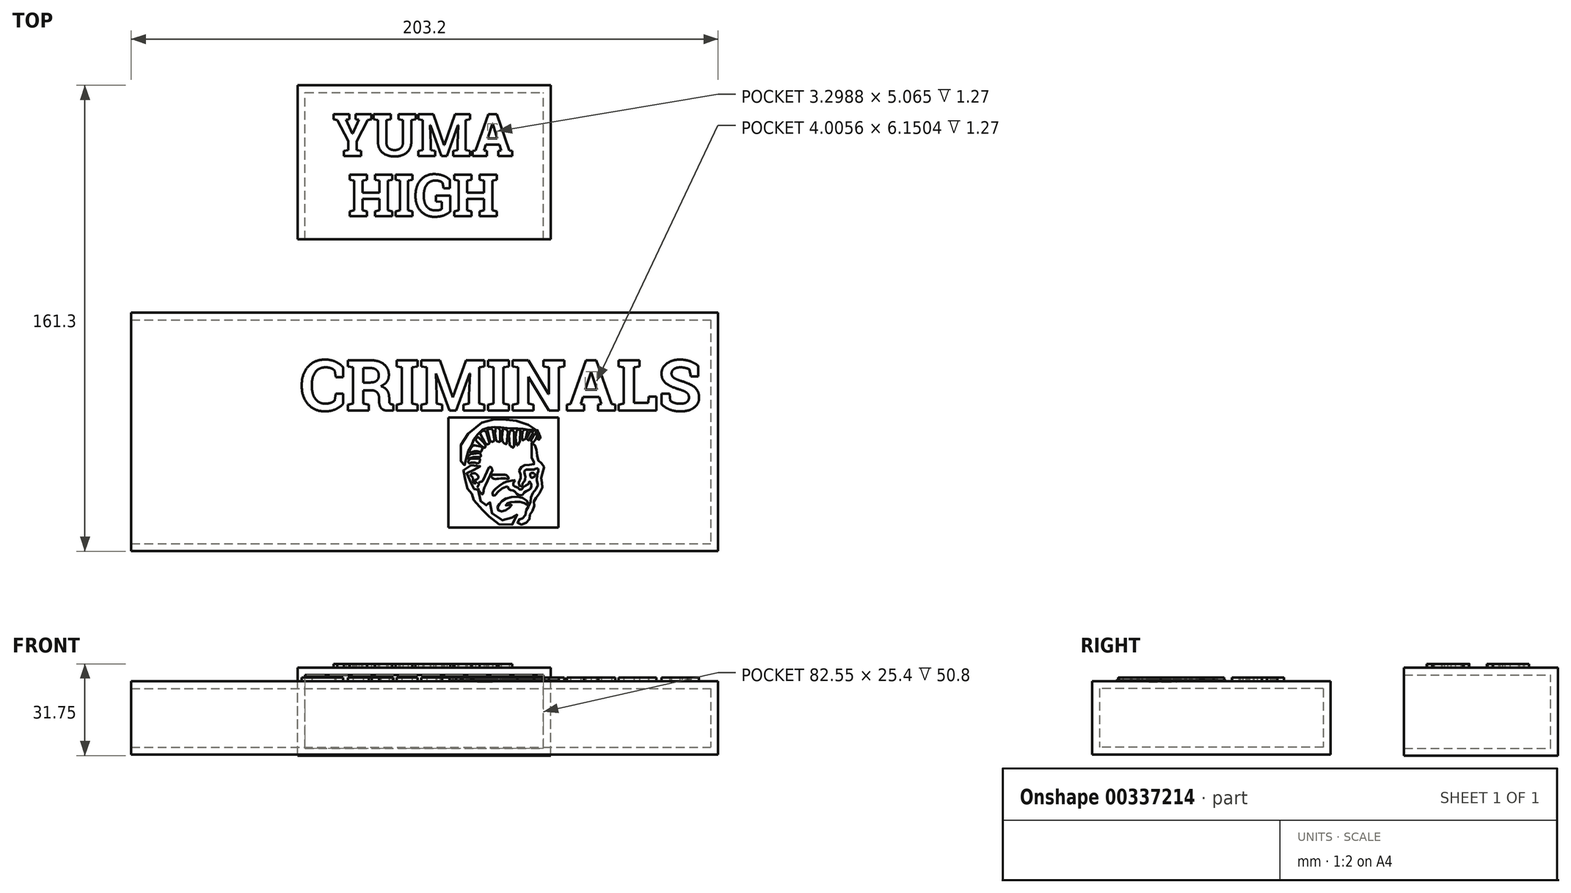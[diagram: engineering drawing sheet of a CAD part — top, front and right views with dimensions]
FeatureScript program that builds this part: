
annotation { "Feature Type Name" : "Feature", "Feature Type Description" : "" }
export const myFeature = defineFeature(function(context is Context, id is Id, definition is map)
    precondition{}
    {
        {
            var Q0;
            Q0=qCreatedBy(makeId("Top.planeOp"),FACE);
            var sketch = newSketch(context, id + "F0", { "sketchPlane" : qUnion([Q0])});
            skLineSegment(sketch, "E0.bottom", {"start": v(-101.6, 41.27) * mm, "end": v(101.6, 41.27) * mm});
            skLineSegment(sketch, "E0.top", {"start": v(-101.6, -41.27) * mm, "end": v(101.6, -41.27) * mm});
            skLineSegment(sketch, "E0.left", {"start": v(-101.6, 41.27) * mm, "end": v(-101.6, -41.27) * mm});
            skLineSegment(sketch, "E0.right", {"start": v(101.6, 41.27) * mm, "end": v(101.6, -41.28) * mm});
            skPoint(sketch, "E0.middle", {"position": v(0, 0) * mm});
            skSolve(sketch);
        }
        {
            var Q0;
            Q0 = qSketchRegion(id + "F0", true);
            extrude(context, id + "F1", {"entities" : qUnion([Q0]), "depth" : 25.4 * mm});
        }
        {
            var Q0;
            Q0=makeQuery(id+"F1.opExtrude","SWEPT_FACE",FACE,{"disambiguationData":[OSD([sQuery(id+"F0.wireOp",EDGE,"E0.left")])]});
            shell(context, id + "F2", {"entities" : qUnion([Q0]), "thickness" : 2.54 * mm});
        }
        {
            var Q0;
            Q0=qCreatedBy(makeId("Right.planeOp"),FACE);
            var sketch = newSketch(context, id + "F3", { "sketchPlane" : qUnion([Q0])});
            skLineSegment(sketch, "E1.bottom", {"start": v(41.28, -47.48) * mm, "end": v(-41.27, -47.48) * mm});
            skLineSegment(sketch, "E1.top", {"start": v(41.27, -72.88) * mm, "end": v(-41.27, -72.88) * mm});
            skLineSegment(sketch, "E1.left", {"start": v(41.28, -47.48) * mm, "end": v(41.27, -72.88) * mm});
            skLineSegment(sketch, "E1.right", {"start": v(-41.27, -47.48) * mm, "end": v(-41.28, -72.88) * mm});
            skPoint(sketch, "E1.middle", {"position": v(0, -60.18) * mm});
            skSolve(sketch);
        }
        {
            var Q0;
            Q0=makeQuery(id+"F3.imprint","IMPRINT",FACE,{"disambiguationData":[TD([[makeQuery(id+"F3.imprint","IMPRINT",EDGE,{"derivedFrom":sQuery(id+"F3.wireOp",EDGE,"E1.bottom")}),1.0]])]});
            extrude(context, id + "F4", {"entities" : qUnion([Q0]), "depth" : 50.8 * mm});
        }
        {
            var Q0;
            Q0=makeQuery(id+"F4.opExtrude","CAP_FACE",FACE,{"disambiguationData":[OSD([sQuery(id+"F3.wireOp",EDGE,"E1.bottom"),sQuery(id+"F3.wireOp",EDGE,"E1.top"),sQuery(id+"F3.wireOp",EDGE,"E1.left"),sQuery(id+"F3.wireOp",EDGE,"E1.right")])],"isStart":false});
            shell(context, id + "F5", {"entities" : qUnion([Q0]), "thickness" : 2.54 * mm, "oppositeDirection" : true});
        }
        {
            var Q0;
            Q0=makeQuery(id+"F4.opExtrude","SWEPT_BODY",BODY,{"disambiguationData":[OSD([sQuery(id+"F3.wireOp",EDGE,"E1.bottom"),sQuery(id+"F3.wireOp",EDGE,"E1.top"),sQuery(id+"F3.wireOp",EDGE,"E1.left"),sQuery(id+"F3.wireOp",EDGE,"E1.right")])]});
            var Q1;
            Q1=makeQuery(id+"F4.opExtrude","CAP_EDGE",EDGE,{"disambiguationData":[OSD([sQuery(id+"F3.wireOp",EDGE,"E1.left")])],"isStart":true});
            transform(context, id + "F6", {"entities" : qUnion([Q0]), "transformType" : TransformType.ROTATION, "transformAxis" : qUnion([Q1]), "angle" : 270 * degree, "makeCopy" : false});
        }
        {
            var Q0;
            Q0=makeQuery(id+"F4.opExtrude","SWEPT_BODY",BODY,{"disambiguationData":[OSD([sQuery(id+"F3.wireOp",EDGE,"E1.bottom"),sQuery(id+"F3.wireOp",EDGE,"E1.top"),sQuery(id+"F3.wireOp",EDGE,"E1.left"),sQuery(id+"F3.wireOp",EDGE,"E1.right")])]});
            transform(context, id + "F7", {"entities" : qUnion([Q0]), "transformType" : TransformType.TRANSLATION_3D, "dx" : -40.9 * mm, "dy" : -81.28 * mm, "dz" : 0 * mm, "makeCopy" : false});
        }
        {
            var Q0;
            Q0=makeQuery(id+"F4.opExtrude","SWEPT_FACE",FACE,{"disambiguationData":[OSD([sQuery(id+"F3.wireOp",EDGE,"E1.top")])]});
            var sketch = newSketch(context, id + "F8", { "sketchPlane" : qUnion([Q0])});
            skText(sketch, "E2", { "text": "YUMA", "fontName": "RobotoSlab-Bold.ttf"});
            skText(sketch, "E3", { "text": "HIGH", "fontName": "RobotoSlab-Bold.ttf"});
            const initialGuessF8  = {"E2": [-0.03137, 0.01307, 1, 0, 0.01456], "E3": [-0.02597, -0.00784, 1, 0, 0.01456]};
            skSetInitialGuess(sketch, initialGuessF8);
            skSolve(sketch);
        }
        {
            var Q0;
            Q0 = qSketchRegion(id + "F8", true);
            extrude(context, id + "F9", {"entities" : qUnion([Q0]), "operationType" : NewBodyOperationType.ADD, "depth" : 1.27 * mm});
        }
        {
            var Q0;
            Q0=makeQuery(id+"F1.opExtrude","CAP_FACE",FACE,{"disambiguationData":[OSD([sQuery(id+"F0.wireOp",EDGE,"E0.bottom"),sQuery(id+"F0.wireOp",EDGE,"E0.top"),sQuery(id+"F0.wireOp",EDGE,"E0.left"),sQuery(id+"F0.wireOp",EDGE,"E0.right")])],"isStart":false});
            var sketch = newSketch(context, id + "F10", { "sketchPlane" : qUnion([Q0])});
            skLineSegment(sketch, "E4.bottom", {"start": v(101.6, -41.28) * mm, "end": v(-48.26, -41.28) * mm});
            skLineSegment(sketch, "E4.top", {"start": v(101.6, 41.27) * mm, "end": v(-48.26, 41.27) * mm});
            skLineSegment(sketch, "E4.left", {"start": v(101.6, -41.28) * mm, "end": v(101.6, 41.28) * mm});
            skLineSegment(sketch, "E4.right", {"start": v(-48.26, -41.28) * mm, "end": v(-48.26, 41.27) * mm});
            skSolve(sketch);
        }
        {
            var Q0;
            Q0=makeQuery(id+"F10.imprint","IMPRINT",FACE,{"disambiguationData":[TD([[makeQuery(id+"F10.imprint","IMPRINT",EDGE,{"derivedFrom":sQuery(id+"F10.wireOp",EDGE,"E4.bottom")}),1.0]])]});
            var sketch = newSketch(context, id + "F11", { "sketchPlane" : qUnion([Q0])});
            skText(sketch, "E5", { "text": "CRIMINALS", "fontName": "RobotoSlab-Bold.ttf"});
            const initialGuessF11  = {"E5": [-0.04318, 0.00738, 1, 0, 0.01768]};
            skSetInitialGuess(sketch, initialGuessF11);
            skSolve(sketch);
        }
        {
            var Q0;
            Q0 = qSketchRegion(id + "F11", true);
            extrude(context, id + "F12", {"entities" : qUnion([Q0]), "operationType" : NewBodyOperationType.ADD, "depth" : 1.27 * mm});
        }
        {
            var Q0;
            Q0=makeQuery(id+"F10.imprint","IMPRINT",FACE,{"disambiguationData":[TD([[makeQuery(id+"F10.imprint","IMPRINT",EDGE,{"derivedFrom":sQuery(id+"F10.wireOp",EDGE,"E4.bottom")}),1.0]])]});
            var sketch = newSketch(context, id + "F13", { "sketchPlane" : qUnion([Q0])});
            skLineSegment(sketch, "E6", {"start": v(25.41, -10.64) * mm, "end": v(30.12, -12.8) * mm});
            skFitSpline(sketch, "E7", {"points": [v(30.12, -12.8) * mm, v(30.12, -13.45) * mm, v(29.01, -13.93) * mm], "startDerivative": vector(0.4, -1.7) * mm, "endDerivative": vector(-2.47, -0.63) * mm});
            skLineSegment(sketch, "E8", {"start": v(29.01, -13.93) * mm, "end": v(23.79, -11.55) * mm});
            skFitSpline(sketch, "E9", {"points": [v(23.79, -11.55) * mm, v(22.65, -11.03) * mm, v(20.72, -10.58) * mm, v(20.68, -10.32) * mm, v(21.24, -9.96) * mm, v(21.33, -9.63) * mm, v(21.67, -9.48) * mm, v(21.88, -9.52) * mm, v(22.1, -9.12) * mm, v(22.33, -9.04) * mm, v(22.6, -9.15) * mm, v(22.79, -8.94) * mm, v(22.93, -8.81) * mm, v(23.24, -8.8) * mm, v(23.79, -9.08) * mm, v(24.23, -9.3) * mm, v(24.36, -9.1) * mm, v(25.04, -9.8) * mm, v(25.02, -10.23) * mm, v(25.41, -10.64) * mm], "startDerivative": vector(-10.89, 6.86) * mm, "endDerivative": vector(9.47, -7.22) * mm});
            skLineSegment(sketch, "E10", {"start": v(17.4, -4.64) * mm, "end": v(19.45, -5.08) * mm});
            skFitSpline(sketch, "E11", {"points": [v(19.45, -5.08) * mm, v(19.86, -5.3) * mm, v(19.97, -5.88) * mm, v(19.73, -6.51) * mm, v(19.45, -6.88) * mm, v(18.23, -6.72) * mm, v(17.48, -6.64) * mm, v(16.69, -6.83) * mm, v(15.64, -6.91) * mm, v(16.64, -4.8) * mm, v(17.4, -4.64) * mm], "startDerivative": vector(6.4, -2.15) * mm, "endDerivative": vector(7.37, -1.37) * mm});
            skLineSegment(sketch, "E12", {"start": v(17.84, -3.06) * mm, "end": v(19.34, -4.6) * mm});
            skLineSegment(sketch, "E13", {"start": v(19.34, -4.6) * mm, "end": v(20.32, -5.26) * mm});
            skFitSpline(sketch, "E14", {"points": [v(20.32, -5.26) * mm, v(20.63, -5.4) * mm, v(21.12, -4.82) * mm, v(18.67, -1.85) * mm, v(18.63, -1.8) * mm, v(18.1, -2) * mm, v(17.68, -2.49) * mm, v(17.84, -3.06) * mm], "startDerivative": vector(2.61, -2.11) * mm, "endDerivative": vector(2.16, -4.54) * mm});
            skLineSegment(sketch, "E15", {"start": v(15.97, -7.65) * mm, "end": v(18.94, -7.28) * mm});
            skFitSpline(sketch, "E16", {"points": [v(18.94, -7.28) * mm, v(19.17, -7.38) * mm, v(19.47, -8.2) * mm, v(19.2, -8.63) * mm, v(18.65, -8.7) * mm], "startDerivative": vector(1.32, -0.15) * mm, "endDerivative": vector(-2.32, 0.1) * mm});
            skLineSegment(sketch, "E17", {"start": v(18.65, -8.7) * mm, "end": v(16.82, -8.7) * mm});
            skLineSegment(sketch, "E18", {"start": v(16.82, -8.7) * mm, "end": v(15.1, -9.24) * mm});
            skFitSpline(sketch, "E19", {"points": [v(15.1, -9.24) * mm, v(14.9, -9.12) * mm, v(15.1, -8.44) * mm, v(15.97, -7.65) * mm], "startDerivative": vector(-1.28, 0.36) * mm, "endDerivative": vector(2.2, 1.6) * mm});
            skLineSegment(sketch, "E20", {"start": v(15.97, -9.25) * mm, "end": v(19.01, -9.25) * mm});
            skFitSpline(sketch, "E21", {"points": [v(19.01, -9.25) * mm, v(19.15, -9.38) * mm, v(18.9, -10.7) * mm], "startDerivative": vector(0.63, -0.29) * mm, "endDerivative": vector(-0.65, -2.3) * mm});
            skLineSegment(sketch, "E22", {"start": v(18.9, -10.7) * mm, "end": v(18.18, -10.8) * mm});
            skLineSegment(sketch, "E23", {"start": v(18.18, -10.8) * mm, "end": v(17.35, -10.6) * mm});
            skLineSegment(sketch, "E24", {"start": v(17.35, -10.6) * mm, "end": v(16.02, -10.6) * mm});
            skFitSpline(sketch, "E25", {"points": [v(16.02, -10.6) * mm, v(15.56, -10.8) * mm, v(15.16, -10.6) * mm, v(15.32, -9.7) * mm, v(15.97, -9.25) * mm], "startDerivative": vector(-2.04, -1.27) * mm, "endDerivative": vector(2.65, 1.08) * mm});
            skLineSegment(sketch, "E26", {"start": v(19.29, -0.72) * mm, "end": v(20.96, -3.7) * mm});
            skLineSegment(sketch, "E27", {"start": v(22.5, -3.7) * mm, "end": v(21.33, 0) * mm});
            skFitSpline(sketch, "E28", {"points": [v(19.29, -0.72) * mm, v(19.29, -0.24) * mm, v(20.47, 0.44) * mm, v(21.33, 0) * mm], "startDerivative": vector(-0.61, 1.88) * mm, "endDerivative": vector(2.16, -2) * mm});
            skFitSpline(sketch, "E29", {"points": [v(20.96, -3.7) * mm, v(21.42, -4.26) * mm, v(22.2, -4.1) * mm, v(22.5, -3.7) * mm], "startDerivative": vector(1.03, -2.04) * mm, "endDerivative": vector(0.68, 1.49) * mm});
            skLineSegment(sketch, "E30", {"start": v(21.75, 0.27) * mm, "end": v(22.6, -2.8) * mm});
            skLineSegment(sketch, "E31", {"start": v(24.12, -2.43) * mm, "end": v(23.55, 0.6) * mm});
            skLineSegment(sketch, "E32", {"start": v(24.62, 1.4) * mm, "end": v(24.38, -0.65) * mm});
            skLineSegment(sketch, "E33", {"start": v(24.38, -0.65) * mm, "end": v(24.69, -2.8) * mm});
            skLineSegment(sketch, "E34", {"start": v(25.08, -3.25) * mm, "end": v(26.14, -3.55) * mm});
            skLineSegment(sketch, "E35", {"start": v(26.14, -3.55) * mm, "end": v(26.14, 0.6) * mm});
            skLineSegment(sketch, "E36", {"start": v(28.81, -0.22) * mm, "end": v(28.47, -3.92) * mm});
            skLineSegment(sketch, "E37", {"start": v(26.99, -3.33) * mm, "end": v(26.77, -1.87) * mm});
            skLineSegment(sketch, "E38", {"start": v(26.77, -1.87) * mm, "end": v(27, 0.57) * mm});
            skLineSegment(sketch, "E39", {"start": v(27.64, 1.07) * mm, "end": v(28.25, 0.76) * mm});
            skLineSegment(sketch, "E40", {"start": v(29.23, -1.06) * mm, "end": v(29.45, -4.37) * mm});
            skLineSegment(sketch, "E41", {"start": v(29.64, -4.83) * mm, "end": v(30.38, -5.33) * mm});
            skLineSegment(sketch, "E42", {"start": v(30.9, 0) * mm, "end": v(30.9, -4.98) * mm});
            skFitSpline(sketch, "E43", {"points": [v(21.75, 0.27) * mm, v(21.75, 0.68) * mm, v(22.41, 1.07) * mm, v(23.22, 0.98) * mm, v(23.55, 0.6) * mm], "startDerivative": vector(-0.5, 2.06) * mm, "endDerivative": vector(1.14, -1.93) * mm});
            skFitSpline(sketch, "E44", {"points": [v(22.6, -2.8) * mm, v(23.09, -3.29) * mm, v(23.9, -3.24) * mm, v(24.12, -2.43) * mm], "startDerivative": vector(1.23, -1.82) * mm, "endDerivative": vector(0.13, 2.8) * mm});
            skFitSpline(sketch, "E45", {"points": [v(24.62, 1.4) * mm, v(24.83, 1.61) * mm, v(25.18, 1.6) * mm, v(26.14, 0.6) * mm], "startDerivative": vector(0.79, 1.04) * mm, "endDerivative": vector(2.02, -2.51) * mm});
            skFitSpline(sketch, "E46", {"points": [v(27, 0.57) * mm, v(27.18, 1.07) * mm, v(27.64, 1.07) * mm], "startDerivative": vector(0.2, 1.2) * mm, "endDerivative": vector(1.1, -0.23) * mm});
            skFitSpline(sketch, "E47", {"points": [v(28.25, 0.76) * mm, v(28.66, 0.37) * mm, v(28.81, -0.22) * mm], "startDerivative": vector(0.97, -0.7) * mm, "endDerivative": vector(0.16, -1.25) * mm});
            skFitSpline(sketch, "E48", {"points": [v(26.99, -3.33) * mm, v(27.64, -3.98) * mm, v(28.25, -4.18) * mm, v(28.47, -3.92) * mm], "startDerivative": vector(1.46, -1.75) * mm, "endDerivative": vector(0.66, 1.36) * mm});
            skFitSpline(sketch, "E49", {"points": [v(29.23, -1.06) * mm, v(29.4, -0.22) * mm, v(29.6, 0.37) * mm, v(30.23, 0.57) * mm, v(30.69, 0.42) * mm, v(30.9, 0) * mm], "startDerivative": vector(0.82, 3.64) * mm, "endDerivative": vector(0.96, -2.68) * mm});
            skFitSpline(sketch, "E50", {"points": [v(30.38, -5.33) * mm, v(30.69, -5.33) * mm, v(30.9, -4.98) * mm], "startDerivative": vector(0.72, -0.15) * mm, "endDerivative": vector(0.34, 0.82) * mm});
            skLineSegment(sketch, "E51", {"start": v(24.69, -2.8) * mm, "end": v(25.08, -3.25) * mm});
            skLineSegment(sketch, "E52", {"start": v(29.45, -4.37) * mm, "end": v(29.64, -4.83) * mm});
            skLineSegment(sketch, "E53", {"start": v(33.17, 0.61) * mm, "end": v(32.95, -3.25) * mm});
            skLineSegment(sketch, "E54", {"start": v(32.95, -3.25) * mm, "end": v(32.23, -4.6) * mm});
            skLineSegment(sketch, "E55", {"start": v(32.23, -4.6) * mm, "end": v(31.95, -4.67) * mm});
            skLineSegment(sketch, "E56", {"start": v(31.95, -4.67) * mm, "end": v(31.71, -3.84) * mm});
            skLineSegment(sketch, "E57", {"start": v(31.71, -3.84) * mm, "end": v(31.5, -1.98) * mm});
            skLineSegment(sketch, "E58", {"start": v(31.5, -1.98) * mm, "end": v(31.69, 0) * mm});
            skLineSegment(sketch, "E59", {"start": v(34.02, 0.4) * mm, "end": v(33.74, -1.09) * mm});
            skLineSegment(sketch, "E60", {"start": v(33.74, -1.09) * mm, "end": v(33.74, -2.59) * mm});
            skLineSegment(sketch, "E61", {"start": v(35, -2.26) * mm, "end": v(35.54, 0) * mm});
            skLineSegment(sketch, "E62", {"start": v(35.54, 0) * mm, "end": v(35.54, 0.16) * mm});
            skLineSegment(sketch, "E63", {"start": v(36.3, -0.17) * mm, "end": v(35.54, -1.83) * mm});
            skLineSegment(sketch, "E64", {"start": v(36.2, -2.76) * mm, "end": v(37.33, -0.78) * mm});
            skLineSegment(sketch, "E65", {"start": v(36.85, -2.76) * mm, "end": v(38.1, -0.56) * mm});
            skLineSegment(sketch, "E66", {"start": v(37.57, -3.63) * mm, "end": v(38.48, -2.59) * mm});
            skLineSegment(sketch, "E67", {"start": v(38.48, -2.59) * mm, "end": v(38.9, -1.28) * mm});
            skLineSegment(sketch, "E68", {"start": v(38.9, -1.28) * mm, "end": v(38.64, -0.54) * mm});
            skLineSegment(sketch, "E69", {"start": v(38.64, -0.54) * mm, "end": v(38.1, -0.56) * mm});
            skLineSegment(sketch, "E70", {"start": v(38.55, 0.66) * mm, "end": v(38.1, 0.16) * mm});
            skLineSegment(sketch, "E71", {"start": v(38.1, 0.16) * mm, "end": v(37.45, 0.74) * mm});
            skLineSegment(sketch, "E72", {"start": v(37.45, 0.74) * mm, "end": v(36.22, 0.74) * mm});
            skFitSpline(sketch, "E73", {"points": [v(31.69, 0) * mm, v(32.1, 0.7) * mm, v(32.63, 0.85) * mm, v(33.17, 0.61) * mm], "startDerivative": vector(0.93, 2.18) * mm, "endDerivative": vector(1.66, -1) * mm});
            skFitSpline(sketch, "E74", {"points": [v(34.02, 0.4) * mm, v(34.32, 0.61) * mm, v(34.78, 0.8) * mm, v(35.33, 0.61) * mm, v(35.54, 0.16) * mm], "startDerivative": vector(1.32, 0.97) * mm, "endDerivative": vector(0.55, -1.97) * mm});
            skFitSpline(sketch, "E75", {"points": [v(33.74, -2.59) * mm, v(34.02, -2.8) * mm, v(35, -2.26) * mm], "startDerivative": vector(0.65, -0.87) * mm, "endDerivative": vector(1.77, 1.32) * mm});
            skFitSpline(sketch, "E76", {"points": [v(35.54, -1.83) * mm, v(35.33, -2.26) * mm, v(35.87, -2.78) * mm, v(36.2, -2.76) * mm], "startDerivative": vector(-1.16, -1.25) * mm, "endDerivative": vector(1.07, 0.37) * mm});
            skFitSpline(sketch, "E77", {"points": [v(36.3, -0.17) * mm, v(36.59, 0.16) * mm, v(37.33, -0.17) * mm, v(37.33, -0.78) * mm], "startDerivative": vector(0.68, 1.56) * mm, "endDerivative": vector(-0.55, -1.93) * mm});
            skFitSpline(sketch, "E78", {"points": [v(36.85, -2.76) * mm, v(37.02, -3.37) * mm, v(37.57, -3.63) * mm], "startDerivative": vector(0.15, -1.38) * mm, "endDerivative": vector(1.29, -0.36) * mm});
            skFitSpline(sketch, "E79", {"points": [v(36.22, 0.74) * mm, v(35.96, 0.74) * mm, v(35.24, 1.22) * mm, v(34.02, 1.1) * mm, v(33.37, 1.1) * mm, v(32.8, 1.35) * mm, v(32.28, 1.3) * mm, v(31.69, 0.92) * mm, v(31.06, 0.96) * mm, v(30.47, 1.14) * mm, v(29.75, 1.14) * mm, v(29.36, 0.92) * mm, v(28.8, 1) * mm, v(28.27, 1.53) * mm, v(27.36, 1.72) * mm, v(26.55, 1.57) * mm, v(25.48, 1.96) * mm, v(24.44, 2.07) * mm, v(24.18, 1.64) * mm, v(23.54, 1.42) * mm, v(22.8, 1.55) * mm, v(21.7, 1.4) * mm, v(21.28, 0.98) * mm, v(20.52, 0.92) * mm, v(19.69, 0.74) * mm, v(18.8, 0.16) * mm, v(18.47, -0.78) * mm, v(17.84, -1.37) * mm, v(17.38, -1.83) * mm, v(17.01, -2.59) * mm, v(16.97, -3.44) * mm, v(16.68, -4.16) * mm, v(16, -4.94) * mm, v(15.5, -5.42) * mm, v(15.12, -6.2) * mm, v(15.12, -7.27) * mm, v(14.72, -8.14) * mm, v(14.44, -8.95) * mm, v(14.46, -10.12) * mm, v(14.03, -11.17) * mm, v(13.44, -11.76) * mm, v(12.83, -11.39) * mm, v(12.57, -9.88) * mm, v(12.55, -4.55) * mm, v(12.57, -4.03) * mm, v(16.22, 0.74) * mm, v(20.26, 3.43) * mm, v(22.87, 4.14) * mm, v(24.37, 4.4) * mm, v(26.44, 4.47) * mm, v(29.31, 4.2) * mm, v(33.35, 3.45) * mm, v(35.84, 2.48) * mm, v(37.33, 1.72) * mm, v(38.55, 0.66) * mm], "startDerivative": vector(-27.73, -7.56) * mm, "endDerivative": vector(53.1, -52.46) * mm});
            skFitSpline(sketch, "E80", {"points": [v(33.87, -18.8) * mm, v(33.6, -18.88) * mm, v(32.86, -18.62) * mm, v(32.48, -18.17) * mm, v(32.62, -17.32) * mm, v(33.14, -16.23) * mm, v(33.4, -15.68) * mm, v(33.3, -15) * mm, v(32.98, -14.38) * mm, v(32.8, -13.29) * mm, v(33.21, -12.32) * mm, v(33.76, -11.83) * mm, v(34.49, -11.5) * mm, v(35.69, -11.39) * mm, v(36.78, -11.32) * mm, v(37.83, -11.16) * mm, v(38.07, -11.1) * mm, v(38.05, -10.82) * mm, v(37.5, -10.22) * mm, v(37, -8.5) * mm, v(37.05, -6.08) * mm, v(37.12, -4.9) * mm, v(36.96, -4.3) * mm, v(36.94, -3.86) * mm, v(37.15, -3.82) * mm, v(37.96, -4.42) * mm, v(38.5, -5.32) * mm, v(38.8, -6.88) * mm, v(39.03, -8.6) * mm, v(39.23, -9.61) * mm, v(40.06, -10.72) * mm, v(40.66, -10.98) * mm, v(41.33, -11.9) * mm, v(40.83, -14.16) * mm, v(40.46, -15.39) * mm, v(40.43, -16.37) * mm, v(40.66, -17.53) * mm], "startDerivative": vector(-14.66, -7.78) * mm, "endDerivative": vector(9.26, -38.03) * mm});
            skFitSpline(sketch, "E81", {"points": [v(40.66, -17.53) * mm, v(40.84, -18.51) * mm, v(40.25, -20.38) * mm, v(39.22, -21.92) * mm, v(38.39, -23.03) * mm, v(37.94, -23.68) * mm, v(37.87, -24.54) * mm, v(37.93, -25.66) * mm, v(37.58, -26.94) * mm, v(36.7, -28.13) * mm, v(36.37, -28.8) * mm, v(36.3, -29.87) * mm, v(36.03, -30.68) * mm, v(34.85, -31.52) * mm, v(33.83, -31.97) * mm, v(32.58, -31.96) * mm, v(32.14, -31.23) * mm, v(32.4, -30.5) * mm, v(33.03, -30.08) * mm, v(33.6, -30.02) * mm, v(34.3, -29.65) * mm, v(34.9, -28.73) * mm, v(35.07, -27.56) * mm, v(35.4, -26.63) * mm, v(35.92, -25.91) * mm, v(36.65, -24.7) * mm, v(36.74, -23.55) * mm, v(36.86, -22.48) * mm, v(37.2, -21.5) * mm, v(38.03, -20.45) * mm, v(38.8, -19.45) * mm, v(39.17, -18.62) * mm, v(38.94, -17.53) * mm, v(38.8, -16.2) * mm, v(38.92, -14.87) * mm], "startDerivative": vector(10.33, -31.8) * mm, "endDerivative": vector(5.32, 40.6) * mm});
            skFitSpline(sketch, "E82", {"points": [v(38.92, -14.87) * mm, v(39.3, -13.87) * mm, v(39.32, -12.74) * mm, v(38.92, -12.54) * mm, v(38.3, -12.84) * mm, v(37.42, -13.04) * mm, v(35.74, -13.05) * mm, v(34.89, -13.18) * mm, v(34.5, -14) * mm, v(34.77, -14.87) * mm, v(34.9, -15.88) * mm, v(34.5, -17.05) * mm, v(34.1, -17.53) * mm, v(33.8, -18.21) * mm, v(33.95, -18.57) * mm, v(33.87, -18.8) * mm], "startDerivative": vector(5.43, 12.1) * mm, "endDerivative": vector(-3.93, -6.24) * mm});
            skFitSpline(sketch, "E83", {"points": [v(36.54, -14.62) * mm, v(36.64, -14.37) * mm, v(37.28, -14.15) * mm, v(38, -14.48) * mm, v(38.29, -15.02) * mm, v(37.91, -15.56) * mm, v(36.95, -15.74) * mm, v(36.5, -15.19) * mm, v(36.54, -14.62) * mm]});
            skFitSpline(sketch, "E84", {"points": [v(35.77, -18.15) * mm, v(36.02, -17.84) * mm, v(36.16, -17.27) * mm, v(36.37, -17.16) * mm, v(36.64, -17.53) * mm, v(36.93, -18.51) * mm, v(36.58, -19.66) * mm, v(35.94, -20.18) * mm, v(35.16, -20.48) * mm, v(34.4, -21.02) * mm, v(34.08, -21.57) * mm, v(33, -21.97) * mm, v(31.87, -21.43) * mm, v(31.3, -20.75) * mm, v(30.77, -20.3) * mm, v(29.74, -20.12) * mm, v(29.07, -19.7) * mm, v(28.86, -18.8) * mm], "startDerivative": vector(7.08, 5.96) * mm, "endDerivative": vector(-1.6, 15.8) * mm});
            skFitSpline(sketch, "E85", {"points": [v(28.86, -18.8) * mm, v(28.62, -18.8) * mm, v(27.66, -19.2) * mm, v(25.87, -20.25) * mm, v(24.13, -22.08) * mm, v(23.76, -22.09) * mm, v(23.6, -21.64) * mm, v(23.52, -20.82) * mm, v(24.08, -20.1) * mm, v(24.92, -19.29) * mm, v(26.92, -17.9) * mm, v(28.24, -17.2) * mm, v(30.86, -16.7) * mm, v(31.16, -16.7) * mm, v(31.23, -16.92) * mm, v(31.04, -17.23) * mm, v(30.88, -17.32) * mm, v(30.74, -17.53) * mm, v(30.67, -18.04) * mm, v(30.76, -18.8) * mm, v(31.5, -18.8) * mm, v(32.44, -19.54) * mm, v(32.86, -19.92) * mm, v(33.37, -19.95) * mm, v(33.87, -19.53) * mm, v(34.31, -19) * mm, v(35.11, -18.51) * mm, v(35.77, -18.15) * mm], "startDerivative": vector(-10.06, 1.52) * mm, "endDerivative": vector(17.39, 10.06) * mm});
            skFitSpline(sketch, "E86", {"points": [v(23.06, -15.45) * mm, v(22.88, -15.13) * mm, v(22.93, -14.86) * mm, v(23.5, -14.74) * mm, v(24.25, -14.75) * mm, v(25.59, -14.78) * mm, v(27.12, -14.77) * mm, v(28.05, -14.8) * mm, v(28.7, -15.38) * mm, v(29.12, -16.02) * mm, v(28.86, -16.22) * mm, v(28.36, -16.15) * mm, v(27.4, -16.07) * mm, v(26, -16.12) * mm, v(25.13, -16.25) * mm, v(24.49, -16.34) * mm, v(23.68, -16.08) * mm, v(23.06, -15.45) * mm]});
            skFitSpline(sketch, "E87", {"points": [v(38.73, -0.24) * mm, v(38.55, 0.16) * mm, v(38.9, 0.66) * mm, v(39.09, 0.66) * mm, v(39.18, 0.16) * mm, v(39.49, -0.17) * mm, v(39.67, -0.5) * mm, v(39.63, -0.78) * mm, v(39.81, -1.01) * mm, v(39.87, -1.5) * mm, v(40.05, -1.84) * mm, v(39.91, -2.3) * mm, v(39.71, -2.38) * mm, v(39.68, -2.66) * mm, v(39.25, -2.5) * mm, v(39.15, -1.97) * mm, v(39.26, -1.63) * mm, v(39.35, -1.03) * mm, v(39.1, -0.6) * mm, v(38.73, -0.24) * mm]});
            skFitSpline(sketch, "E88", {"points": [v(18.54, -20.05) * mm, v(18.65, -19.41) * mm, v(18.47, -19.14) * mm, v(18.01, -19.41) * mm, v(17.26, -19.73) * mm, v(16.51, -19.82) * mm, v(16.13, -19.8) * mm, v(16.13, -18.7) * mm, v(15.95, -17.34) * mm, v(15.5, -16.1) * mm, v(14.7, -14.7) * mm, v(14.56, -13.78) * mm, v(15.04, -13.14) * mm, v(16.22, -13.1) * mm, v(17.56, -13.23) * mm, v(18.51, -13.16) * mm, v(19.2, -12.55) * mm, v(19.1, -11.55) * mm, v(17.97, -11.26) * mm, v(16.79, -11.3) * mm, v(15.76, -11.55) * mm, v(14.45, -11.55) * mm, v(13.65, -12.69) * mm, v(13.1, -13.91) * mm, v(13.31, -15.37) * mm, v(13.95, -16.41) * mm, v(14.38, -17.03) * mm, v(14.65, -17.69) * mm, v(14.74, -18.91) * mm, v(14.86, -20.53) * mm, v(15, -21.2) * mm, v(15.83, -21.52) * mm, v(16.4, -21.32) * mm, v(16.72, -21.27) * mm, v(16.88, -21.64) * mm, v(16.7, -22.1) * mm, v(17.13, -23.75) * mm, v(18.2, -25.3) * mm, v(19.83, -26.77) * mm, v(21.44, -27.84) * mm, v(21.72, -27.95) * mm, v(22.08, -28.84) * mm, v(22.78, -30.14) * mm, v(24.33, -31.34) * mm, v(26.6, -32.13) * mm, v(29.06, -32.2) * mm, v(30.49, -31.93) * mm, v(31.76, -30.64) * mm, v(32.15, -29.05) * mm, v(31.7, -28.25) * mm, v(31.26, -28.14) * mm, v(30.58, -28.7) * mm, v(30.15, -29.7) * mm, v(29.8, -30.27) * mm, v(28.44, -30.59) * mm, v(26.7, -30.54) * mm, v(24.99, -29.86) * mm, v(23.52, -28.45) * mm, v(22.92, -26.1) * mm, v(22.74, -24.93) * mm, v(22.58, -24.3) * mm, v(21.8, -23.91) * mm, v(21.38, -24) * mm, v(21.26, -24.86) * mm, v(21.33, -25.55) * mm, v(21.29, -25.73) * mm, v(20.99, -25.66) * mm, v(20.04, -24.68) * mm, v(18.95, -23.34) * mm, v(18.38, -21.82) * mm, v(18.54, -20.05) * mm]});
            skFitSpline(sketch, "E89", {"points": [v(17.4, -17.87) * mm, v(16.9, -17.48) * mm, v(16.72, -16.14) * mm, v(16.47, -15.55) * mm, v(15.92, -15.19) * mm, v(15.92, -14.75) * mm, v(16.8, -14.28) * mm, v(18.06, -14.64) * mm, v(18.58, -15.82) * mm, v(18.01, -16.4) * mm, v(17.54, -16.62) * mm, v(17.38, -17.07) * mm, v(17.72, -17.41) * mm, v(17.9, -17.34) * mm, v(17.8, -17.64) * mm, v(17.4, -17.87) * mm]});
            skFitSpline(sketch, "E90", {"points": [v(28.85, -25.36) * mm, v(28.12, -25.55) * mm, v(28.2, -25.11) * mm, v(29.2, -24.57) * mm, v(30.28, -24.3) * mm, v(32.65, -24.2) * mm, v(34.58, -24.66) * mm, v(35.58, -25.3) * mm, v(35.8, -25.23) * mm, v(35.9, -24.96) * mm, v(34.87, -23.27) * mm, v(32.1, -22.48) * mm, v(28.76, -22.89) * mm, v(26.62, -24.1) * mm, v(25.65, -25.16) * mm, v(25.15, -26.27) * mm, v(25.85, -27.4) * mm, v(27.3, -27.39) * mm, v(29.03, -26.45) * mm, v(30.06, -25.43) * mm, v(30.15, -25.02) * mm, v(29.56, -25.11) * mm, v(28.85, -25.36) * mm]});
            skSolve(sketch);
        }
        {
            var Q0;
            Q0 = qSketchRegion(id + "F13", true);
            extrude(context, id + "F14", {"entities" : qUnion([Q0]), "depth" : 1.27 * mm});
        }
        {
            var Q0;
            Q0=qCreatedBy(makeId("Front.planeOp"),FACE);
            var sketch = newSketch(context, id + "F15", { "sketchPlane" : qUnion([Q0])});
            skLineSegment(sketch, "E91", {"start": v(26.54, 36.74) * mm, "end": v(26.54, 53.6) * mm});
            skSolve(sketch);
        }
        {
            var Q0;
            Q0=makeQuery(id+"F10.imprint","IMPRINT",FACE,{"disambiguationData":[TD([[makeQuery(id+"F10.imprint","IMPRINT",EDGE,{"derivedFrom":sQuery(id+"F10.wireOp",EDGE,"E4.bottom")}),1.0]])]});
            var sketch = newSketch(context, id + "F16", { "sketchPlane" : qUnion([Q0])});
            skLineSegment(sketch, "E92.bottom", {"start": v(8.23, 5.03) * mm, "end": v(46.33, 5.03) * mm});
            skLineSegment(sketch, "E92.top", {"start": v(8.23, -33.07) * mm, "end": v(46.33, -33.07) * mm});
            skLineSegment(sketch, "E92.left", {"start": v(8.23, 5.03) * mm, "end": v(8.23, -33.07) * mm});
            skLineSegment(sketch, "E92.right", {"start": v(46.33, 5.03) * mm, "end": v(46.33, -33.07) * mm});
            skSolve(sketch);
        }
        {
            var Q0;
            Q0 = qSketchRegion(id + "F16", true);
            extrude(context, id + "F17", {"entities" : qUnion([Q0]), "depth" : 0.25 * mm});
        }
        {
            var Q0;
            Q0=makeQuery(id+"F14.opExtrude","SWEPT_BODY",BODY,{"disambiguationData":[OSD([sQuery(id+"F13.wireOp",EDGE,"E6"),sQuery(id+"F13.wireOp",EDGE,"E7"),sQuery(id+"F13.wireOp",EDGE,"E8"),sQuery(id+"F13.wireOp",EDGE,"E9")])]});
            var Q1;
            Q1=sQuery(id+"F15.wireOp",EDGE,"E91");
            transform(context, id + "F18", {"entities" : qUnion([Q0]), "transformType" : TransformType.ROTATION, "transformAxis" : qUnion([Q1]), "angle" : 90 * degree, "makeCopy" : false});
        }
        {
            var Q0;
            Q0=makeQuery(id+"F14.opExtrude","SWEPT_BODY",BODY,{"disambiguationData":[OSD([sQuery(id+"F13.wireOp",EDGE,"E6"),sQuery(id+"F13.wireOp",EDGE,"E7"),sQuery(id+"F13.wireOp",EDGE,"E8"),sQuery(id+"F13.wireOp",EDGE,"E9")])]});
            transform(context, id + "F19", {"entities" : qUnion([Q0]), "transformType" : TransformType.TRANSLATION_3D, "dx" : -17.02 * mm, "dy" : -15.75 * mm, "dz" : -0.25 * mm, "makeCopy" : false});
        }
        {
            var Q0;
            Q0=makeQuery(id+"F4.opExtrude","SWEPT_BODY",BODY,{"disambiguationData":[OSD([sQuery(id+"F3.wireOp",EDGE,"E1.bottom"),sQuery(id+"F3.wireOp",EDGE,"E1.top"),sQuery(id+"F3.wireOp",EDGE,"E1.left"),sQuery(id+"F3.wireOp",EDGE,"E1.right")])]});
            var Q1;
            Q1=makeQuery(id+"F1.opExtrude","CAP_EDGE",EDGE,{"disambiguationData":[OSD([sQuery(id+"F0.wireOp",EDGE,"E0.left")])],"isStart":true});
            transform(context, id + "F20", {"entities" : qUnion([Q0]), "transformType" : TransformType.ROTATION, "transformAxis" : qUnion([Q1]), "angle" : 180 * degree, "oppositeDirection" : true, "makeCopy" : false});
        }
        {
            var Q0;
            Q0=makeQuery(id+"F4.opExtrude","SWEPT_BODY",BODY,{"disambiguationData":[OSD([sQuery(id+"F3.wireOp",EDGE,"E1.bottom"),sQuery(id+"F3.wireOp",EDGE,"E1.top"),sQuery(id+"F3.wireOp",EDGE,"E1.left"),sQuery(id+"F3.wireOp",EDGE,"E1.right")])]});
            var Q1;
            Q1=makeQuery(id+"F1.opExtrude","SWEPT_EDGE",EDGE,{"disambiguationData":[OSD([sQuery(id+"F0.wireOp",EDGE,"E0.bottom"),sQuery(id+"F0.wireOp",EDGE,"E0.left")])]});
            var Q2;
            Q2=makeQuery(id+"F1.opExtrude","SWEPT_EDGE",EDGE,{"disambiguationData":[OSD([sQuery(id+"F0.wireOp",EDGE,"E0.bottom"),sQuery(id+"F0.wireOp",EDGE,"E0.left")])]});
            transform(context, id + "F21", {"entities" : qUnion([Q0]), "transformType" : TransformType.ROTATION, "transformAxis" : qUnion([Q2]), "angle" : 90 * degree, "makeCopy" : false});
        }
        {
            var Q0;
            Q0=makeQuery(id+"F4.opExtrude","SWEPT_BODY",BODY,{"disambiguationData":[OSD([sQuery(id+"F3.wireOp",EDGE,"E1.bottom"),sQuery(id+"F3.wireOp",EDGE,"E1.top"),sQuery(id+"F3.wireOp",EDGE,"E1.left"),sQuery(id+"F3.wireOp",EDGE,"E1.right")])]});
            transform(context, id + "F22", {"entities" : qUnion([Q0]), "transformType" : TransformType.TRANSLATION_3D, "dx" : 0 * mm, "dy" : -144.27 * mm, "dz" : -49.02 * mm, "makeCopy" : false});
        }
        {
            var Q0;
            Q0=makeQuery(id+"F4.opExtrude","SWEPT_BODY",BODY,{"disambiguationData":[OSD([sQuery(id+"F3.wireOp",EDGE,"E1.bottom"),sQuery(id+"F3.wireOp",EDGE,"E1.top"),sQuery(id+"F3.wireOp",EDGE,"E1.left"),sQuery(id+"F3.wireOp",EDGE,"E1.right")])]});
            var Q1;
            Q1=makeQuery(id+"F1.opExtrude","SWEPT_EDGE",EDGE,{"disambiguationData":[OSD([sQuery(id+"F0.wireOp",EDGE,"E0.bottom"),sQuery(id+"F0.wireOp",EDGE,"E0.left")])]});
            transform(context, id + "F23", {"entities" : qUnion([Q0]), "transformType" : TransformType.ROTATION, "transformAxis" : qUnion([Q1]), "angle" : 90 * degree, "makeCopy" : false});
        }
        {
            var Q0;
            Q0=makeQuery(id+"F4.opExtrude","SWEPT_BODY",BODY,{"disambiguationData":[OSD([sQuery(id+"F3.wireOp",EDGE,"E1.bottom"),sQuery(id+"F3.wireOp",EDGE,"E1.top"),sQuery(id+"F3.wireOp",EDGE,"E1.left"),sQuery(id+"F3.wireOp",EDGE,"E1.right")])]});
            transform(context, id + "F24", {"entities" : qUnion([Q0]), "transformType" : TransformType.TRANSLATION_3D, "dx" : 143.76 * mm, "dy" : 0 * mm, "dz" : 3.8 * mm, "makeCopy" : false});
        }
    });
